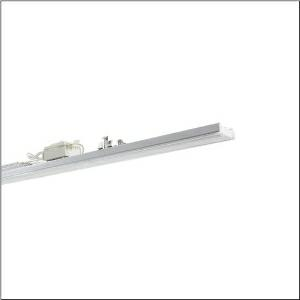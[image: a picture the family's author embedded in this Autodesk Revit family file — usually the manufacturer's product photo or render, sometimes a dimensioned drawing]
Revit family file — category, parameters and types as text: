
# Revit family: licross_21_recessed_mo_52tl12dn68xg
name_source: partatom
category: Lighting Fixtures
units: mm (PartAtom-declared; Revit-internal decimal feet)

## family parameters
Cut with Voids When Loaded = No
Host = Face
Light Source = No
Part Type = Normal
Room Calculation Point = No
Round Connector Dimension = Use Diameter
Shared = No

## types (1)
- --- (1 x LED, 8000 lm, 45.6 W, 6500K)
    Apparent Load = 46 VA
    CIE Flux Codes = 72 92 99 100 100
    Color Rendering = 80
    Color Temperature = 6500K
    Default Elevation = 1800 mm
    Description = Licross 21 Recessed MO, luminaire insert, of sheet steel, galvanised, coil coated, white, length: 1.500mm, width: 66mm, height: 67mm, LED rated luminous flux: 8.000lm, light colour: 865, SDCM (Standard Deviation of Colour Matching)MacAdam ≤ 3 SDCM (initial), control gear: DALI 2, with plug, 5-pole, with phase selection, mains connection: 220..240V, AC, 50/60Hz, rated input power: 46W, internal wiring halogen-free, primary optical cover: cover, of PMMA, light emission: direct distribution, primary light characteristic: symmetric, protection rating (complete): IP40, insulation class (complete): insulation class I (protective earthing), certification: CE, ENEC, VDE, UKCA, protection symbol: D if used in an environment without relevant dust loads with corresponding accessories, impact resistance: IK06, permissible ambient temperature for indoor applications: -25..+40°C, corresponds to IFS (International Featured Standards) requirements for safety and quality in the food industry, reducing of maximum allowable ambient temperature of 5°C with ceiling mounting, LABS conformity tested according to VDMA 24364:2018-05, The light source and the operating device comply with the requirements of the Ecodesign Regulation (EU) 2019/2020 and are replaceable in accordance with this regulation, packaging unit: 1 piece
    Height = 58 mm
    Lamp = 1 x LED
    Lamp Light Flux = 8000 lm
    Lamp Power = 45.6 W
    Lamp count = 1
    Length = 1500 mm
    Luminous efficacy = 175 lm/W
    Manufacturer = Siteco
    ModVariant = No
    Model = 52TL12DN68XG
    Mounting Place = Ceiling
    Mounting Type = Pendant
    Number of Poles = 1
    OnlyDefault = Yes
    Power Factor = 1
    Product Name = Licross 21 Recessed MO
    Product group = luminaire insert | ceiling pendant
    ProductGroupID = 901
    Protection Class = Protection class I
    Protection Degree = IP 40
    RLX_Detail_Level = 1
    RLX_Emergency_Light_Flux = 0 lm
    RLX_Emergency_Type = 0
    RLX_Emergency_Type_DB = No
    RlxData = <blob elided: 24785 chars, md5=c1bd06c1>
    Socket = socket
    Standby Power = 0 W
    System Light Flux = 8000 lm
    System Power = 46 W
    Type Comments = factory setting: luminous flux: 100 % | dim-lin: 254 | 306 mA
    Type Image = l_1296930.jpg
    URL = http://relux.com
    VarID = @adj_030113
    Voltage = 0 V
    Weight = 0.00 kg
    Width = 66 mm

## geometry (parser evidence)
native form markers: Blend x4, Sweep x11
no freeform markers — native parametric forms only
